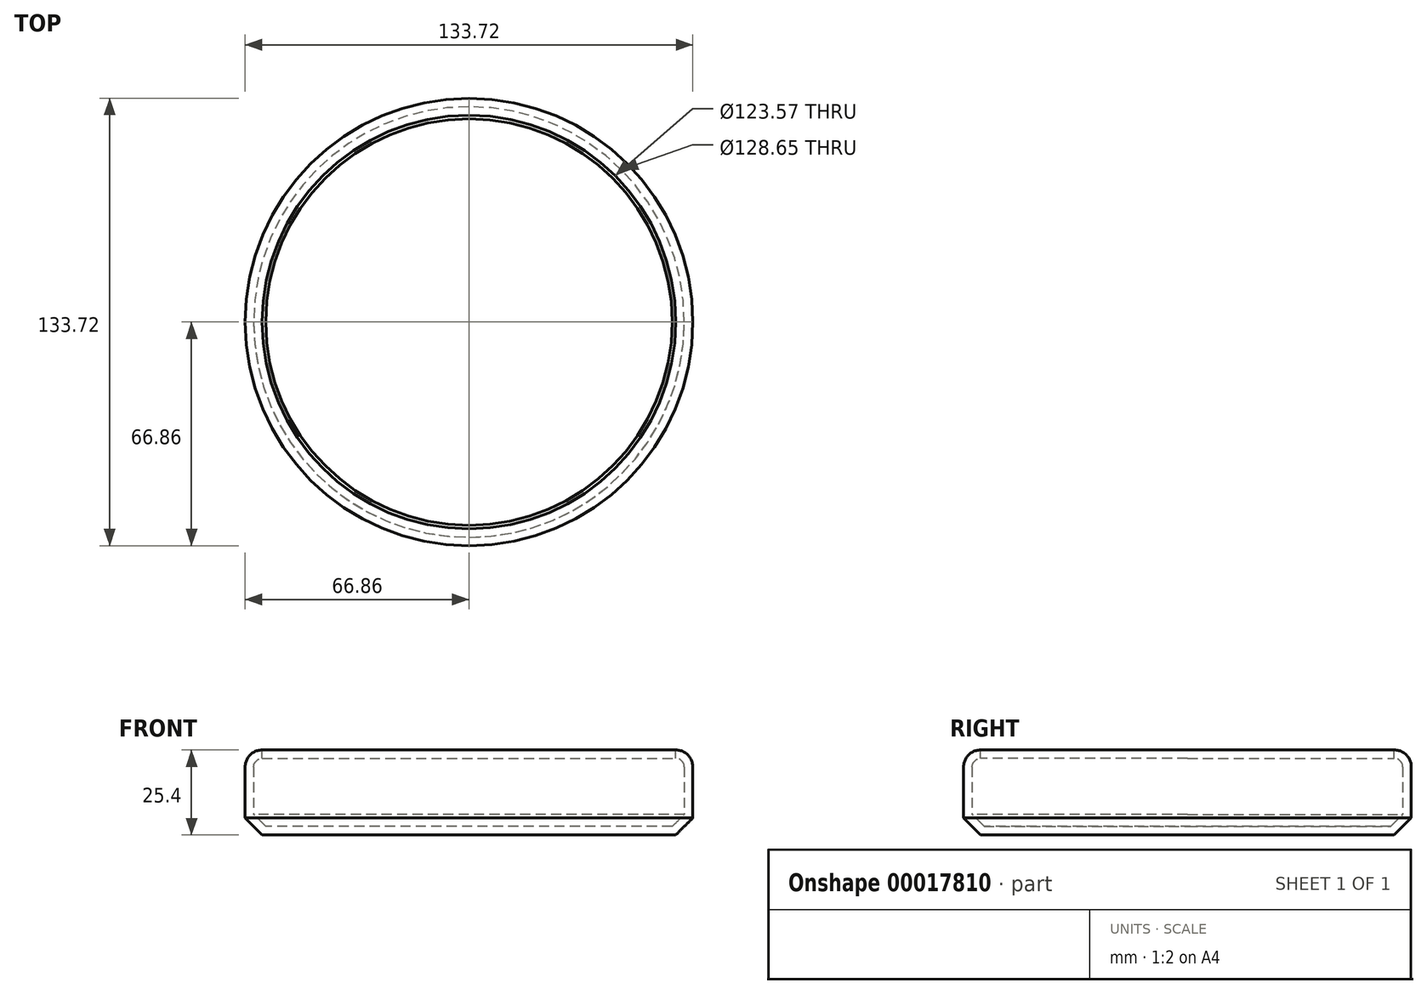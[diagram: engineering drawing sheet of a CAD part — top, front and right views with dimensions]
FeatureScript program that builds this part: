
annotation { "Feature Type Name" : "Feature", "Feature Type Description" : "" }
export const myFeature = defineFeature(function(context is Context, id is Id, definition is map)
    precondition{}
    {
        {
            var Q0;
            Q0=qCreatedBy(makeId("Top.planeOp"),FACE);
            var sketch = newSketch(context, id + "F0", { "sketchPlane" : qUnion([Q0])});
            skCircle(sketch, "E0", {"center": v(0, 0) * mm, "radius": 66.86 * mm});
            skSolve(sketch);
        }
        {
            var Q0;
            Q0 = qSketchRegion(id + "F0", true);
            extrude(context, id + "F1", {"entities" : qUnion([Q0]), "depth" : 25.4 * mm});
        }
        {
            var Q0;
            Q0=makeQuery(id+"F1.opExtrude","CAP_FACE",FACE,{"disambiguationData":[OSD([sQuery(id+"F0.wireOp",EDGE,"E0")])],"isStart":false});
            fillet(context, id + "F2", {"entities" : qUnion([Q0]), "radius" : 5.08 * mm, "tangentPropagation" : true, "allowEdgeOverflow" : false});
        }
        {
            var Q0;
            Q0=makeQuery(id+"F1.opExtrude","CAP_FACE",FACE,{"disambiguationData":[OSD([sQuery(id+"F0.wireOp",EDGE,"E0")])],"isStart":true});
            chamfer(context, id + "F3", {"entities" : qUnion([Q0]), "width" : 5.08 * mm, "tangentPropagation" : true});
        }
        {
            var Q0;
            Q0=makeQuery(id+"F1.opExtrude","CAP_FACE",FACE,{"disambiguationData":[OSD([sQuery(id+"F0.wireOp",EDGE,"E0")])],"isStart":false});
            shell(context, id + "F4", {"entities" : qUnion([Q0]), "thickness" : 2.54 * mm});
        }
    });
